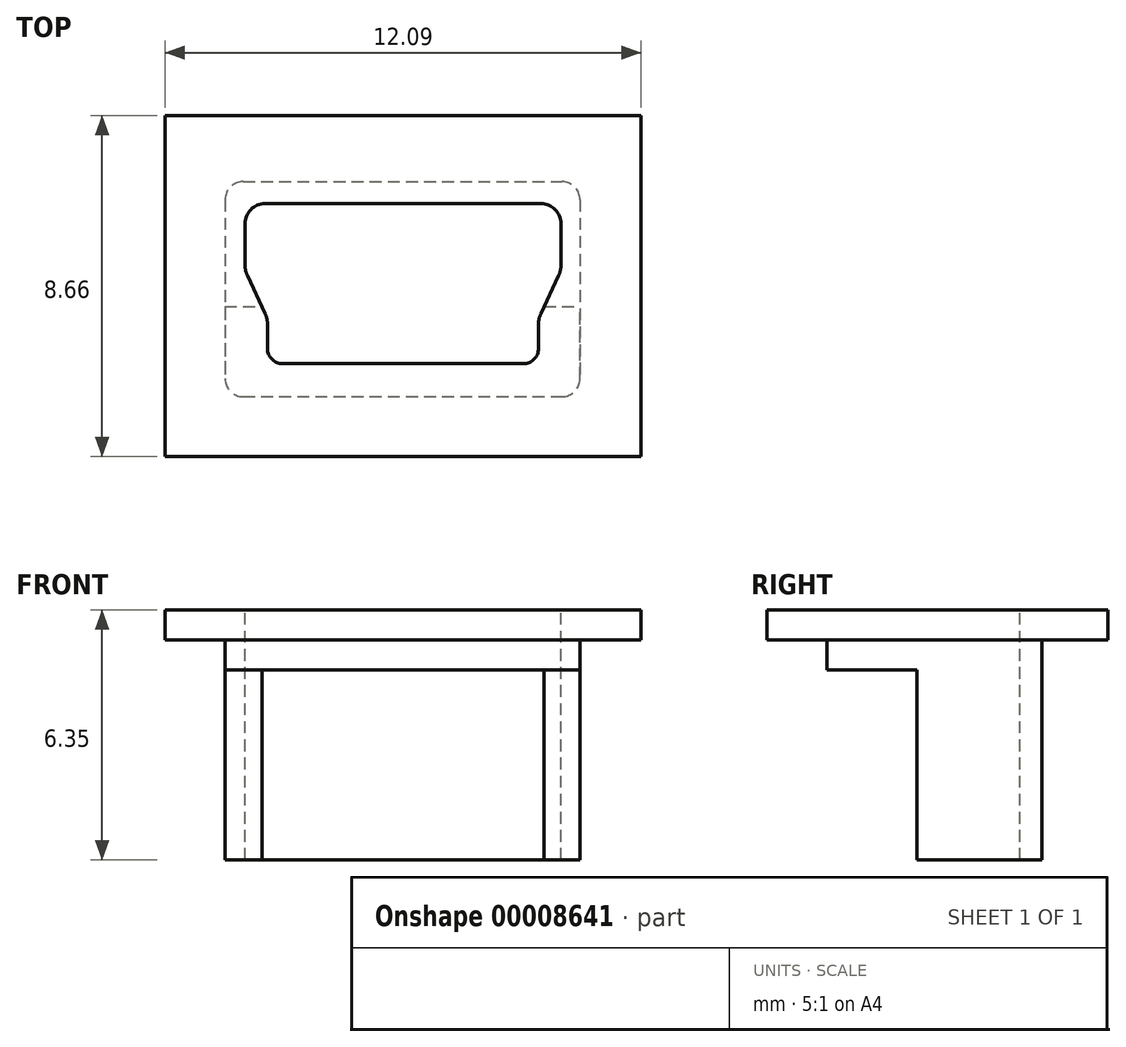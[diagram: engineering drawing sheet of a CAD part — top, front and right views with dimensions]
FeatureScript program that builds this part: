
annotation { "Feature Type Name" : "Feature", "Feature Type Description" : "" }
export const myFeature = defineFeature(function(context is Context, id is Id, definition is map)
    precondition{}
    {
        {
            var Q0;
            Q0=qCreatedBy(makeId("Top.planeOp"),FACE);
            var sketch = newSketch(context, id + "F0", { "sketchPlane" : qUnion([Q0])});
            skLineSegment(sketch, "E0.rect.bottom", {"start": v(-4.5, 2.73) * mm, "end": v(4.5, 2.73) * mm});
            skLineSegment(sketch, "E0.rect.top", {"start": v(-4.5, -2.73) * mm, "end": v(4.5, -2.73) * mm});
            skLineSegment(sketch, "E0.rect.left", {"start": v(-4.5, 2.73) * mm, "end": v(-4.5, -2.73) * mm});
            skLineSegment(sketch, "E0.rect.right", {"start": v(4.5, 2.73) * mm, "end": v(4.5, -2.73) * mm});
            skPoint(sketch, "E0.rect.middle", {"position": v(0, 0) * mm});
            skLineSegment(sketch, "E1.bottom", {"start": v(-4, 2.17) * mm, "end": v(4.03, 2.17) * mm});
            skLineSegment(sketch, "E1.top", {"start": v(-3.43, -1.9) * mm, "end": v(3.45, -1.9) * mm});
            skLineSegment(sketch, "E1.left", {"start": v(-4, 2.17) * mm, "end": v(-4, 0.47) * mm});
            skLineSegment(sketch, "E1.right", {"start": v(4.03, 2.17) * mm, "end": v(4.03, 0.47) * mm});
            skLineSegment(sketch, "E2.left", {"start": v(-3.43, -1.9) * mm, "end": v(-3.43, -0.75) * mm});
            skLineSegment(sketch, "E2.right", {"start": v(3.45, -1.9) * mm, "end": v(3.45, -0.75) * mm});
            skLineSegment(sketch, "E3", {"start": v(4.03, 0.47) * mm, "end": v(3.45, -0.75) * mm});
            skLineSegment(sketch, "E4", {"start": v(-4, 0.47) * mm, "end": v(-3.43, -0.75) * mm});
            skLineSegment(sketch, "E5.bottom", {"start": v(-6.03, 4.4) * mm, "end": v(6.06, 4.4) * mm});
            skLineSegment(sketch, "E5.top", {"start": v(-6.03, -4.25) * mm, "end": v(6.06, -4.25) * mm});
            skLineSegment(sketch, "E5.left", {"start": v(-6.03, 4.4) * mm, "end": v(-6.03, -4.25) * mm});
            skLineSegment(sketch, "E5.right", {"start": v(6.06, 4.4) * mm, "end": v(6.06, -4.25) * mm});
            skSolve(sketch);
        }
        {
            var Q0;
            Q0=makeQuery(id+"F0.imprint","IMPRINT",FACE,{"disambiguationData":[TD([[makeQuery(id+"F0.imprint","IMPRINT",EDGE,{"derivedFrom":sQuery(id+"F0.wireOp",EDGE,"E0.rect.bottom")}),-1.0]])]});
            extrude(context, id + "F1", {"entities" : qUnion([Q0]), "oppositeDirection" : true, "depth" : 6.35 * mm});
        }
        {
            var Q0;
            Q0=makeQuery(id+"F1.opExtrude","SWEPT_EDGE",EDGE,{"disambiguationData":[OSD([sQuery(id+"F0.wireOp",EDGE,"E1.bottom"),sQuery(id+"F0.wireOp",EDGE,"E1.left")])]});
            var Q1;
            Q1=makeQuery(id+"F1.opExtrude","SWEPT_EDGE",EDGE,{"disambiguationData":[OSD([sQuery(id+"F0.wireOp",EDGE,"E1.bottom"),sQuery(id+"F0.wireOp",EDGE,"E1.right")])]});
            fillet(context, id + "F2", {"entities" : qUnion([Q0, Q1]), "radius" : 0.5 * mm, "tangentPropagation" : true, "allowEdgeOverflow" : false});
        }
        {
            var Q0;
            Q0=makeQuery(id+"F1.opExtrude","SWEPT_EDGE",EDGE,{"disambiguationData":[OSD([sQuery(id+"F0.wireOp",EDGE,"E1.left"),sQuery(id+"F0.wireOp",EDGE,"E4")])]});
            var Q1;
            Q1=makeQuery(id+"F1.opExtrude","SWEPT_EDGE",EDGE,{"disambiguationData":[OSD([sQuery(id+"F0.wireOp",EDGE,"E2.left"),sQuery(id+"F0.wireOp",EDGE,"E4")])]});
            var Q2;
            Q2=makeQuery(id+"F1.opExtrude","SWEPT_EDGE",EDGE,{"disambiguationData":[OSD([sQuery(id+"F0.wireOp",EDGE,"E2.right"),sQuery(id+"F0.wireOp",EDGE,"E3")])]});
            var Q3;
            Q3=makeQuery(id+"F1.opExtrude","SWEPT_EDGE",EDGE,{"disambiguationData":[OSD([sQuery(id+"F0.wireOp",EDGE,"E1.right"),sQuery(id+"F0.wireOp",EDGE,"E3")])]});
            fillet(context, id + "F3", {"entities" : qUnion([Q0, Q1, Q2, Q3]), "radius" : 0.64 * mm, "tangentPropagation" : true, "allowEdgeOverflow" : false});
        }
        {
            var Q0;
            Q0=makeQuery(id+"F1.opExtrude","SWEPT_EDGE",EDGE,{"disambiguationData":[OSD([sQuery(id+"F0.wireOp",EDGE,"E1.top"),sQuery(id+"F0.wireOp",EDGE,"E2.left")])]});
            var Q1;
            Q1=makeQuery(id+"F1.opExtrude","SWEPT_EDGE",EDGE,{"disambiguationData":[OSD([sQuery(id+"F0.wireOp",EDGE,"E1.top"),sQuery(id+"F0.wireOp",EDGE,"E2.right")])]});
            fillet(context, id + "F4", {"entities" : qUnion([Q0, Q1]), "radius" : 0.38 * mm, "tangentPropagation" : true, "allowEdgeOverflow" : false});
        }
        {
            var Q0;
            Q0 = qSketchRegion(id + "F0", true);
            extrude(context, id + "F5", {"entities" : qUnion([Q0]), "operationType" : NewBodyOperationType.ADD, "oppositeDirection" : true, "depth" : 0.76 * mm});
        }
        {
            var Q0;
            Q0=makeQuery(id+"F1.opExtrude","SWEPT_EDGE",EDGE,{"disambiguationData":[OSD([sQuery(id+"F0.wireOp",EDGE,"E0.rect.top"),sQuery(id+"F0.wireOp",EDGE,"E0.rect.right")])]});
            var Q1;
            Q1=makeQuery(id+"F1.opExtrude","SWEPT_EDGE",EDGE,{"disambiguationData":[OSD([sQuery(id+"F0.wireOp",EDGE,"E0.rect.top"),sQuery(id+"F0.wireOp",EDGE,"E0.rect.left")])]});
            var Q2;
            Q2=makeQuery(id+"F1.opExtrude","SWEPT_EDGE",EDGE,{"disambiguationData":[OSD([sQuery(id+"F0.wireOp",EDGE,"E0.rect.bottom"),sQuery(id+"F0.wireOp",EDGE,"E0.rect.left")])]});
            var Q3;
            Q3=makeQuery(id+"F1.opExtrude","SWEPT_EDGE",EDGE,{"disambiguationData":[OSD([sQuery(id+"F0.wireOp",EDGE,"E0.rect.bottom"),sQuery(id+"F0.wireOp",EDGE,"E0.rect.right")])]});
            fillet(context, id + "F6", {"entities" : qUnion([Q0, Q1, Q2, Q3]), "radius" : 0.46 * mm, "tangentPropagation" : true, "allowEdgeOverflow" : false});
        }
        {
            var Q0;
            Q0=makeQuery(id+"F1.opExtrude","SWEPT_FACE",FACE,{"disambiguationData":[OSD([sQuery(id+"F0.wireOp",EDGE,"E0.rect.right")])]});
            var sketch = newSketch(context, id + "F7", { "sketchPlane" : qUnion([Q0])});
            skLineSegment(sketch, "E6.bottom", {"start": v(-2.73, -1.52) * mm, "end": v(-0.44, -1.52) * mm});
            skLineSegment(sketch, "E6.top", {"start": v(-2.73, -6.35) * mm, "end": v(-0.44, -6.35) * mm});
            skLineSegment(sketch, "E6.left", {"start": v(-2.73, -1.52) * mm, "end": v(-2.73, -6.35) * mm});
            skLineSegment(sketch, "E6.right", {"start": v(-0.44, -1.52) * mm, "end": v(-0.44, -6.35) * mm});
            skSolve(sketch);
        }
        {
            var Q0;
            {var subQ6=sQuery(id+"F7.wireOp",EDGE,"E6.right");Q0=makeQuery(id+"F7.imprint","IMPRINT",FACE,{"disambiguationData":[TD([[makeQuery(id+"F7.imprint","IMPRINT",EDGE,{"derivedFrom":subQ6}),-1.0]])]});}
            var Q1;
            {var subQ6=sQuery(id+"F7.wireOp",EDGE,"E6.left");Q1=makeQuery(id+"F7.imprint","IMPRINT",FACE,{"disambiguationData":[TD([[makeQuery(id+"F7.imprint","IMPRINT",EDGE,{"derivedFrom":subQ6}),1.0]])]});}
            extrude(context, id + "F8", {"entities" : qUnion([Q0, Q1]), "operationType" : NewBodyOperationType.REMOVE, "oppositeDirection" : true, "depth" : 13.24 * mm});
        }
    });
